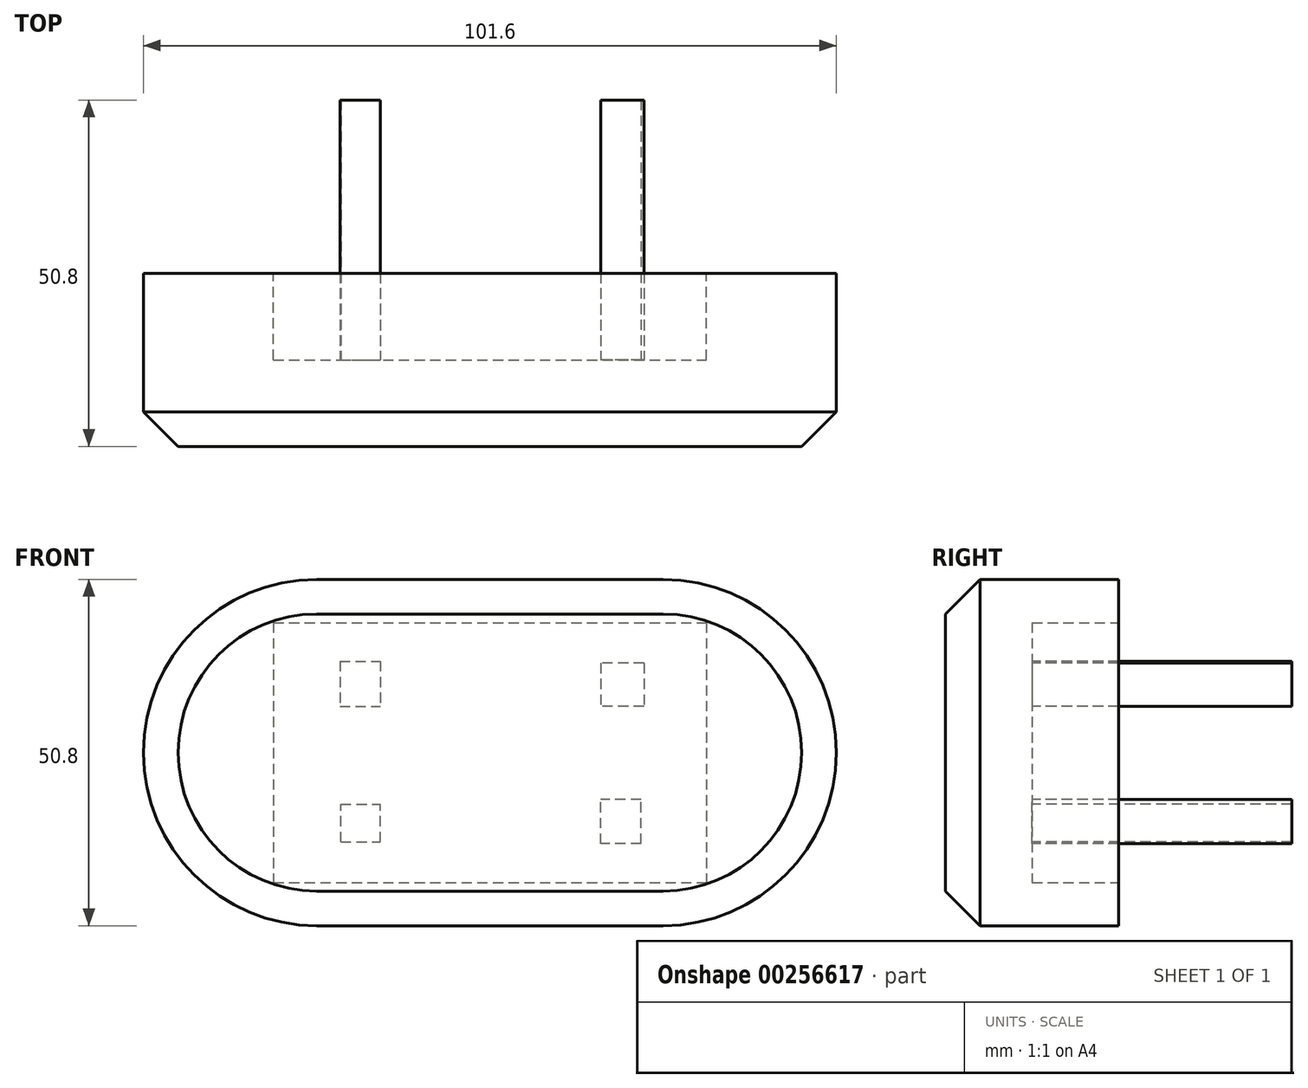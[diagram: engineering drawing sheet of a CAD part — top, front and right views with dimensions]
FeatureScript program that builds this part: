
annotation { "Feature Type Name" : "Feature", "Feature Type Description" : "" }
export const myFeature = defineFeature(function(context is Context, id is Id, definition is map)
    precondition{}
    {
        {
            var Q0;
            Q0=qCreatedBy(makeId("Front.planeOp"),FACE);
            var sketch = newSketch(context, id + "F0", { "sketchPlane" : qUnion([Q0])});
            skLineSegment(sketch, "E0.bottom", {"start": v(-25.4, -25.4) * mm, "end": v(25.4, -25.4) * mm});
            skLineSegment(sketch, "E0.top", {"start": v(-25.4, 25.4) * mm, "end": v(25.4, 25.4) * mm});
            skLineSegment(sketch, "E0.left", {"start": v(-50.8, 0) * mm, "end": v(-50.8, 0) * mm});
            skLineSegment(sketch, "E0.right", {"start": v(50.8, 0) * mm, "end": v(50.8, 0) * mm});
            skPoint(sketch, "E0.middle", {"position": v(0, 0) * mm});
            skPoint(sketch, "E1.visualSharp", {"position": v(50.8, 25.4) * mm});
            skArc(sketch, "E1.filletArc", {"start": v(50.8, 0) * mm, "mid": v(43.36, 17.96) * mm, "end": v(25.4, 25.4) * mm});
            skPoint(sketch, "E2.visualSharp", {"position": v(50.8, -25.4) * mm});
            skArc(sketch, "E2.filletArc", {"start": v(25.4, -25.4) * mm, "mid": v(43.36, -17.96) * mm, "end": v(50.8, 0) * mm});
            skPoint(sketch, "E3.visualSharp", {"position": v(-50.8, -25.4) * mm});
            skArc(sketch, "E3.filletArc", {"start": v(-50.8, 0) * mm, "mid": v(-43.36, -17.96) * mm, "end": v(-25.4, -25.4) * mm});
            skPoint(sketch, "E4.visualSharp", {"position": v(-50.8, 25.4) * mm});
            skArc(sketch, "E4.filletArc", {"start": v(-25.4, 25.4) * mm, "mid": v(-43.36, 17.96) * mm, "end": v(-50.8, 0) * mm});
            skSolve(sketch);
        }
        {
            var Q0;
            Q0=makeQuery(id+"F0.imprint","IMPRINT",FACE,{"disambiguationData":[TD([[makeQuery(id+"F0.imprint","IMPRINT",EDGE,{"derivedFrom":sQuery(id+"F0.wireOp",EDGE,"E0.bottom")}),1.0]])]});
            extrude(context, id + "F1", {"entities" : qUnion([Q0]), "depth" : 25.4 * mm});
        }
        {
            var Q0;
            Q0=qCreatedBy(makeId("Front.planeOp"),FACE);
            var sketch = newSketch(context, id + "F2", { "sketchPlane" : qUnion([Q0])});
            skLineSegment(sketch, "E5.bottom", {"start": v(-31.75, 19.05) * mm, "end": v(31.75, 19.05) * mm});
            skLineSegment(sketch, "E5.top", {"start": v(-31.75, -19.05) * mm, "end": v(31.75, -19.05) * mm});
            skLineSegment(sketch, "E5.left", {"start": v(-31.75, 19.05) * mm, "end": v(-31.75, -19.05) * mm});
            skLineSegment(sketch, "E5.right", {"start": v(31.75, 19.05) * mm, "end": v(31.75, -19.05) * mm});
            skPoint(sketch, "E5.middle", {"position": v(0, 0) * mm});
            skSolve(sketch);
        }
        {
            var Q0;
            Q0 = qSketchRegion(id + "F2", true);
            extrude(context, id + "F3", {"entities" : qUnion([Q0]), "operationType" : NewBodyOperationType.REMOVE, "depth" : 12.7 * mm});
        }
        {
            var Q0;
            Q0=makeQuery(id+"F3.boolean.opBoolean","COPY",EDGE,{"derivedFrom":makeQuery(id+"F3.opExtrude","CAP_EDGE",EDGE,{"disambiguationData":[OSD([sQuery(id+"F2.wireOp",EDGE,"E5.bottom")])],"isStart":true})});
            var Q1;
            Q1=makeQuery(id+"F3.boolean.opBoolean","COPY",EDGE,{"derivedFrom":makeQuery(id+"F3.opExtrude","CAP_EDGE",EDGE,{"disambiguationData":[OSD([sQuery(id+"F2.wireOp",EDGE,"E5.left")])],"isStart":true})});
            var Q2;
            Q2=makeQuery(id+"F3.boolean.opBoolean","COPY",EDGE,{"derivedFrom":makeQuery(id+"F3.opExtrude","CAP_EDGE",EDGE,{"disambiguationData":[OSD([sQuery(id+"F2.wireOp",EDGE,"E5.top")])],"isStart":true})});
            var Q3;
            Q3=makeQuery(id+"F3.boolean.opBoolean","COPY",EDGE,{"derivedFrom":makeQuery(id+"F3.opExtrude","CAP_EDGE",EDGE,{"disambiguationData":[OSD([sQuery(id+"F2.wireOp",EDGE,"E5.right")])],"isStart":true})});
            var Q4;
            Q4=makeQuery(id+"F1.opExtrude","CAP_EDGE",EDGE,{"disambiguationData":[OSD([sQuery(id+"F0.wireOp",EDGE,"E0.top")])],"isStart":false});
            chamfer(context, id + "F4", {"entities" : qUnion([Q0, Q1, Q2, Q3, Q4]), "width" : 5.08 * mm, "tangentPropagation" : true});
        }
        {
            var Q0;
            Q0=qCreatedBy(makeId("Front.planeOp"),FACE);
            var sketch = newSketch(context, id + "F5", { "sketchPlane" : qUnion([Q0])});
            skLineSegment(sketch, "E6.bottom", {"start": v(22.59, 13.11) * mm, "end": v(16.24, 13.11) * mm});
            skLineSegment(sketch, "E6.top", {"start": v(22.59, 6.76) * mm, "end": v(16.24, 6.76) * mm});
            skLineSegment(sketch, "E6.left", {"start": v(22.59, 13.11) * mm, "end": v(22.59, 6.76) * mm});
            skLineSegment(sketch, "E6.right", {"start": v(16.24, 13.11) * mm, "end": v(16.24, 6.76) * mm});
            skLineSegment(sketch, "E7.bottom", {"start": v(-22, 13.4) * mm, "end": v(-16.06, 13.4) * mm});
            skLineSegment(sketch, "E7.top", {"start": v(-22, 6.76) * mm, "end": v(-16.06, 6.76) * mm});
            skLineSegment(sketch, "E7.left", {"start": v(-22, 13.4) * mm, "end": v(-22, 6.76) * mm});
            skLineSegment(sketch, "E7.right", {"start": v(-16.06, 13.4) * mm, "end": v(-16.06, 6.76) * mm});
            skLineSegment(sketch, "E8.bottom", {"start": v(22.18, -13.4) * mm, "end": v(16.24, -13.4) * mm});
            skLineSegment(sketch, "E8.top", {"start": v(22.18, -6.9) * mm, "end": v(16.24, -6.9) * mm});
            skLineSegment(sketch, "E8.left", {"start": v(22.18, -13.4) * mm, "end": v(22.18, -6.9) * mm});
            skLineSegment(sketch, "E8.right", {"start": v(16.24, -13.4) * mm, "end": v(16.24, -6.9) * mm});
            skLineSegment(sketch, "E9.bottom", {"start": v(-21.86, -13.11) * mm, "end": v(-16.06, -13.11) * mm});
            skLineSegment(sketch, "E9.top", {"start": v(-21.86, -7.6) * mm, "end": v(-16.06, -7.6) * mm});
            skLineSegment(sketch, "E9.left", {"start": v(-21.86, -13.11) * mm, "end": v(-21.86, -7.6) * mm});
            skLineSegment(sketch, "E9.right", {"start": v(-16.06, -13.11) * mm, "end": v(-16.06, -7.6) * mm});
            skSolve(sketch);
        }
        {
            var Q0;
            Q0=makeQuery(id+"F5.imprint","IMPRINT",FACE,{"disambiguationData":[TD([[makeQuery(id+"F5.imprint","IMPRINT",EDGE,{"derivedFrom":sQuery(id+"F5.wireOp",EDGE,"E6.bottom")}),1.0]])]});
            var Q1;
            Q1=makeQuery(id+"F5.imprint","IMPRINT",FACE,{"disambiguationData":[TD([[makeQuery(id+"F5.imprint","IMPRINT",EDGE,{"derivedFrom":sQuery(id+"F5.wireOp",EDGE,"E8.bottom")}),-1.0]])]});
            var Q2;
            Q2=makeQuery(id+"F5.imprint","IMPRINT",FACE,{"disambiguationData":[TD([[makeQuery(id+"F5.imprint","IMPRINT",EDGE,{"derivedFrom":sQuery(id+"F5.wireOp",EDGE,"E9.bottom")}),1.0]])]});
            var Q3;
            Q3=makeQuery(id+"F5.imprint","IMPRINT",FACE,{"disambiguationData":[TD([[makeQuery(id+"F5.imprint","IMPRINT",EDGE,{"derivedFrom":sQuery(id+"F5.wireOp",EDGE,"E7.bottom")}),-1.0]])]});
            extrude(context, id + "F6", {"entities" : qUnion([Q0, Q1, Q2, Q3]), "operationType" : NewBodyOperationType.ADD, "endBound" : BoundingType.SYMMETRIC, "oppositeDirection" : true, "depth" : 50.8 * mm});
        }
    });
